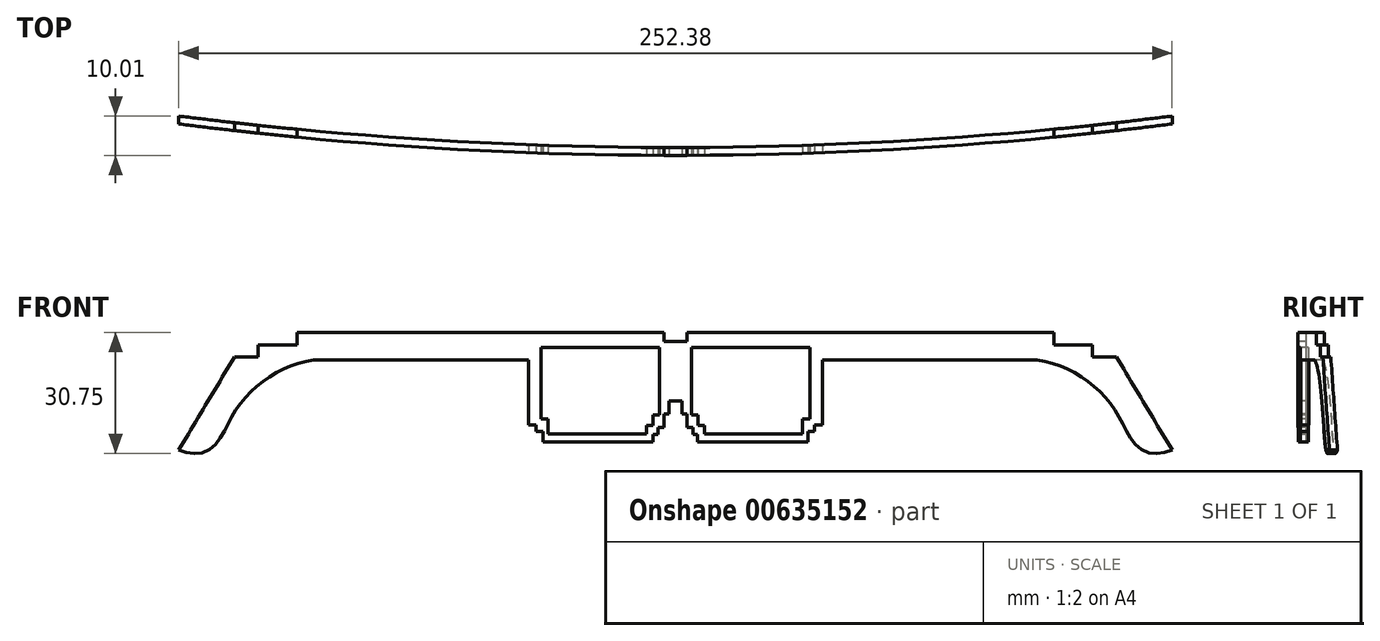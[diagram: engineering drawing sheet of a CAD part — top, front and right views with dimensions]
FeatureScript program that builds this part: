
annotation { "Feature Type Name" : "Feature", "Feature Type Description" : "" }
export const myFeature = defineFeature(function(context is Context, id is Id, definition is map)
    precondition{}
    {
        {
            var Q0;
            Q0=qCreatedBy(makeId("Top.planeOp"),FACE);
            var sketch = newSketch(context, id + "F0", { "sketchPlane" : qUnion([Q0])});
            skCircle(sketch, "E0", {"center": v(0, 1000) * mm, "radius": 1000 * mm});
            skCircle(sketch, "E1.0", {"center": v(0, 1000) * mm, "radius": 998 * mm});
            skSolve(sketch);
        }
        {
            var Q0;
            Q0 = qSketchRegion(id + "F0", true);
            extrude(context, id + "F1", {"entities" : qUnion([Q0]), "endBound" : BoundingType.SYMMETRIC, "depth" : 50 * mm, "offsetDistance" : 25 * mm});
        }
        {
            var Q0;
            Q0=qCreatedBy(makeId("Front.planeOp"),FACE);
            var sketch = newSketch(context, id + "F2", { "sketchPlane" : qUnion([Q0])});
            skLineSegment(sketch, "E2", {"start": v(0, 0) * mm, "end": v(0, 49.82) * mm, "construction": true});
            skLineSegment(sketch, "E3", {"start": v(0, 0) * mm, "end": v(1.62, 0) * mm});
            skLineSegment(sketch, "E4", {"start": v(1.62, 0) * mm, "end": v(1.62, -3.29) * mm});
            skLineSegment(sketch, "E5", {"start": v(1.62, -3.29) * mm, "end": v(2.95, -3.29) * mm});
            skLineSegment(sketch, "E6", {"start": v(2.95, -3.29) * mm, "end": v(2.95, -6.77) * mm});
            skLineSegment(sketch, "E7", {"start": v(2.95, -6.77) * mm, "end": v(4.46, -6.77) * mm});
            skLineSegment(sketch, "E8", {"start": v(4.46, -6.77) * mm, "end": v(4.46, -8.49) * mm});
            skLineSegment(sketch, "E9", {"start": v(4.46, -8.49) * mm, "end": v(5.66, -8.49) * mm});
            skLineSegment(sketch, "E10", {"start": v(5.66, -8.49) * mm, "end": v(5.66, -10.45) * mm});
            skLineSegment(sketch, "E11", {"start": v(5.66, -10.45) * mm, "end": v(33.62, -10.45) * mm});
            skLineSegment(sketch, "E12", {"start": v(33.62, -10.45) * mm, "end": v(33.62, -7.75) * mm});
            skLineSegment(sketch, "E13", {"start": v(33.62, -7.75) * mm, "end": v(35.37, -7.75) * mm});
            skLineSegment(sketch, "E14", {"start": v(35.37, -7.75) * mm, "end": v(35.37, -6.12) * mm});
            skLineSegment(sketch, "E15", {"start": v(35.37, -6.12) * mm, "end": v(37.33, -6.12) * mm});
            skLineSegment(sketch, "E16", {"start": v(37.33, -6.12) * mm, "end": v(37.33, 10.5) * mm});
            skLineSegment(sketch, "E17", {"start": v(37.33, 10.5) * mm, "end": v(39.1, 10.5) * mm});
            skLineSegment(sketch, "E18", {"start": v(39.1, 10.5) * mm, "end": v(39.1, 17.42) * mm, "construction": true});
            skLineSegment(sketch, "E19", {"start": v(39.1, 17.42) * mm, "end": v(2.95, 17.42) * mm});
            skLineSegment(sketch, "E20", {"start": v(2.95, 17.42) * mm, "end": v(2.95, 15.2) * mm});
            skLineSegment(sketch, "E21", {"start": v(2.95, 15.2) * mm, "end": v(0, 15.2) * mm});
            skLineSegment(sketch, "E22", {"start": v(4.1, -3.59) * mm, "end": v(4.1, 13.63) * mm});
            skLineSegment(sketch, "E23", {"start": v(4.1, 13.63) * mm, "end": v(34.18, 13.63) * mm});
            skLineSegment(sketch, "E24", {"start": v(34.18, 13.63) * mm, "end": v(34.18, -4.56) * mm});
            skLineSegment(sketch, "E25", {"start": v(34.18, -4.56) * mm, "end": v(32.32, -4.56) * mm});
            skLineSegment(sketch, "E26", {"start": v(32.32, -4.56) * mm, "end": v(32.32, -8.39) * mm});
            skLineSegment(sketch, "E27", {"start": v(32.32, -8.39) * mm, "end": v(7.41, -8.39) * mm});
            skLineSegment(sketch, "E28", {"start": v(7.41, -8.39) * mm, "end": v(7.41, -6.19) * mm});
            skLineSegment(sketch, "E29", {"start": v(7.41, -6.19) * mm, "end": v(5.67, -6.19) * mm});
            skLineSegment(sketch, "E30", {"start": v(5.67, -6.19) * mm, "end": v(5.67, -3.53) * mm});
            skLineSegment(sketch, "E31", {"start": v(5.67, -3.53) * mm, "end": v(4.1, -3.59) * mm});
            skLineSegment(sketch, "E32.MirrorCS", {"start": v(-4.46, -8.49) * mm, "end": v(-5.66, -8.49) * mm});
            skLineSegment(sketch, "E33.MirrorCS", {"start": v(-5.66, -8.49) * mm, "end": v(-5.66, -10.45) * mm});
            skLineSegment(sketch, "E34.MirrorCS", {"start": v(-4.46, -6.77) * mm, "end": v(-4.46, -8.49) * mm});
            skLineSegment(sketch, "E35.MirrorCS", {"start": v(-2.95, -6.77) * mm, "end": v(-4.46, -6.77) * mm});
            skLineSegment(sketch, "E36.MirrorCS", {"start": v(-7.41, -6.19) * mm, "end": v(-5.67, -6.19) * mm});
            skLineSegment(sketch, "E37.MirrorCS", {"start": v(-1.62, -3.29) * mm, "end": v(-2.95, -3.29) * mm});
            skLineSegment(sketch, "E38.MirrorCS", {"start": v(-33.62, -7.75) * mm, "end": v(-35.37, -7.75) * mm});
            skLineSegment(sketch, "E39.MirrorCS", {"start": v(0, 0) * mm, "end": v(-1.62, 0) * mm});
            skLineSegment(sketch, "E40.MirrorCS", {"start": v(-35.37, -7.75) * mm, "end": v(-35.37, -6.12) * mm});
            skLineSegment(sketch, "E41.MirrorCS", {"start": v(-34.18, -4.56) * mm, "end": v(-32.32, -4.56) * mm});
            skLineSegment(sketch, "E42.MirrorCS", {"start": v(-37.33, 10.5) * mm, "end": v(-39.1, 10.5) * mm});
            skLineSegment(sketch, "E43.MirrorCS", {"start": v(-35.37, -6.12) * mm, "end": v(-37.33, -6.12) * mm});
            skLineSegment(sketch, "E44.MirrorCS", {"start": v(-7.41, -8.39) * mm, "end": v(-7.41, -6.19) * mm});
            skLineSegment(sketch, "E45.MirrorCS", {"start": v(-2.95, 17.42) * mm, "end": v(-2.95, 15.2) * mm});
            skLineSegment(sketch, "E46.MirrorCS", {"start": v(-5.66, -10.45) * mm, "end": v(-33.62, -10.45) * mm});
            skLineSegment(sketch, "E47.MirrorCS", {"start": v(-2.95, -3.29) * mm, "end": v(-2.95, -6.77) * mm});
            skLineSegment(sketch, "E48.MirrorCS", {"start": v(-33.62, -10.45) * mm, "end": v(-33.62, -7.75) * mm});
            skLineSegment(sketch, "E49.MirrorCS", {"start": v(-32.32, -8.39) * mm, "end": v(-7.41, -8.39) * mm});
            skLineSegment(sketch, "E50.MirrorCS", {"start": v(-1.62, 0) * mm, "end": v(-1.62, -3.29) * mm});
            skLineSegment(sketch, "E51.MirrorCS", {"start": v(-37.33, -6.12) * mm, "end": v(-37.33, 10.5) * mm});
            skLineSegment(sketch, "E52.MirrorCS", {"start": v(-34.18, 13.63) * mm, "end": v(-34.18, -4.56) * mm});
            skLineSegment(sketch, "E53.MirrorCS", {"start": v(-4.1, -3.59) * mm, "end": v(-4.1, 13.63) * mm});
            skLineSegment(sketch, "E54.MirrorCS", {"start": v(-32.32, -4.56) * mm, "end": v(-32.32, -8.39) * mm});
            skLineSegment(sketch, "E55.MirrorCS", {"start": v(-4.1, 13.63) * mm, "end": v(-34.18, 13.63) * mm});
            skLineSegment(sketch, "E56.MirrorCS", {"start": v(-5.67, -6.19) * mm, "end": v(-5.67, -3.53) * mm});
            skLineSegment(sketch, "E57.MirrorCS", {"start": v(-39.1, 10.5) * mm, "end": v(-39.1, 17.42) * mm});
            skLineSegment(sketch, "E58.MirrorCS", {"start": v(-2.95, 15.2) * mm, "end": v(0, 15.2) * mm});
            skLineSegment(sketch, "E59.MirrorCS", {"start": v(-5.67, -3.53) * mm, "end": v(-4.1, -3.59) * mm});
            skLineSegment(sketch, "E60.MirrorCS", {"start": v(-39.1, 17.42) * mm, "end": v(-2.95, 17.42) * mm});
            skLineSegment(sketch, "E61", {"start": v(39.1, 10.5) * mm, "end": v(89.86, 10.5) * mm});
            skLineSegment(sketch, "E62", {"start": v(39.1, 17.42) * mm, "end": v(96.1, 17.42) * mm});
            skLineSegment(sketch, "E63", {"start": v(96.1, 17.42) * mm, "end": v(96.1, 14.22) * mm});
            skLineSegment(sketch, "E64", {"start": v(96.1, 14.22) * mm, "end": v(105.97, 14.22) * mm});
            skLineSegment(sketch, "E65", {"start": v(105.97, 14.22) * mm, "end": v(105.97, 11.21) * mm});
            skLineSegment(sketch, "E66", {"start": v(105.97, 11.21) * mm, "end": v(112.05, 11.21) * mm});
            skLineSegment(sketch, "E67", {"start": v(112.05, 11.21) * mm, "end": v(126.2, -12.44) * mm});
            skFitSpline(sketch, "E68", {"points": [v(126.2, -12.44) * mm, v(115.6, -9.36) * mm, v(110.05, 0) * mm, v(89.86, 10.5) * mm], "startDerivative": vector(-60.92, -23.5) * mm, "endDerivative": vector(-59.48, 0) * mm});
            skLineSegment(sketch, "E69.MirrorCS", {"start": v(-96.1, 17.42) * mm, "end": v(-96.1, 14.22) * mm});
            skLineSegment(sketch, "E70.MirrorCS", {"start": v(-105.97, 14.22) * mm, "end": v(-105.97, 11.21) * mm});
            skLineSegment(sketch, "E71.MirrorCS", {"start": v(-39.1, 17.42) * mm, "end": v(-96.1, 17.42) * mm});
            skLineSegment(sketch, "E72.MirrorCS", {"start": v(-39.1, 10.5) * mm, "end": v(-39.1, 17.42) * mm, "construction": true});
            skLineSegment(sketch, "E73.MirrorCS", {"start": v(-39.1, 10.5) * mm, "end": v(-89.86, 10.5) * mm});
            skLineSegment(sketch, "E74.MirrorCS", {"start": v(-96.1, 14.22) * mm, "end": v(-105.97, 14.22) * mm});
            skLineSegment(sketch, "E75.MirrorCS", {"start": v(-112.05, 11.21) * mm, "end": v(-126.2, -12.44) * mm});
            skLineSegment(sketch, "E76.MirrorCS", {"start": v(-105.97, 11.21) * mm, "end": v(-112.05, 11.21) * mm});
            skFitSpline(sketch, "E77.MirrorCS", {"points": [v(-126.2, -12.44) * mm, v(-115.6, -9.36) * mm, v(-110.05, 0) * mm, v(-89.86, 10.5) * mm], "startDerivative": vector(60.92, -23.5) * mm, "endDerivative": vector(59.48, 0) * mm});
            skSolve(sketch);
        }
        {
            var Q0;
            Q0 = qSketchRegion(id + "F2", true);
            extrude(context, id + "F3", {"entities" : qUnion([Q0]), "operationType" : NewBodyOperationType.INTERSECT, "oppositeDirection" : true, "depth" : 25 * mm, "offsetDistance" : 25 * mm});
        }
    });
